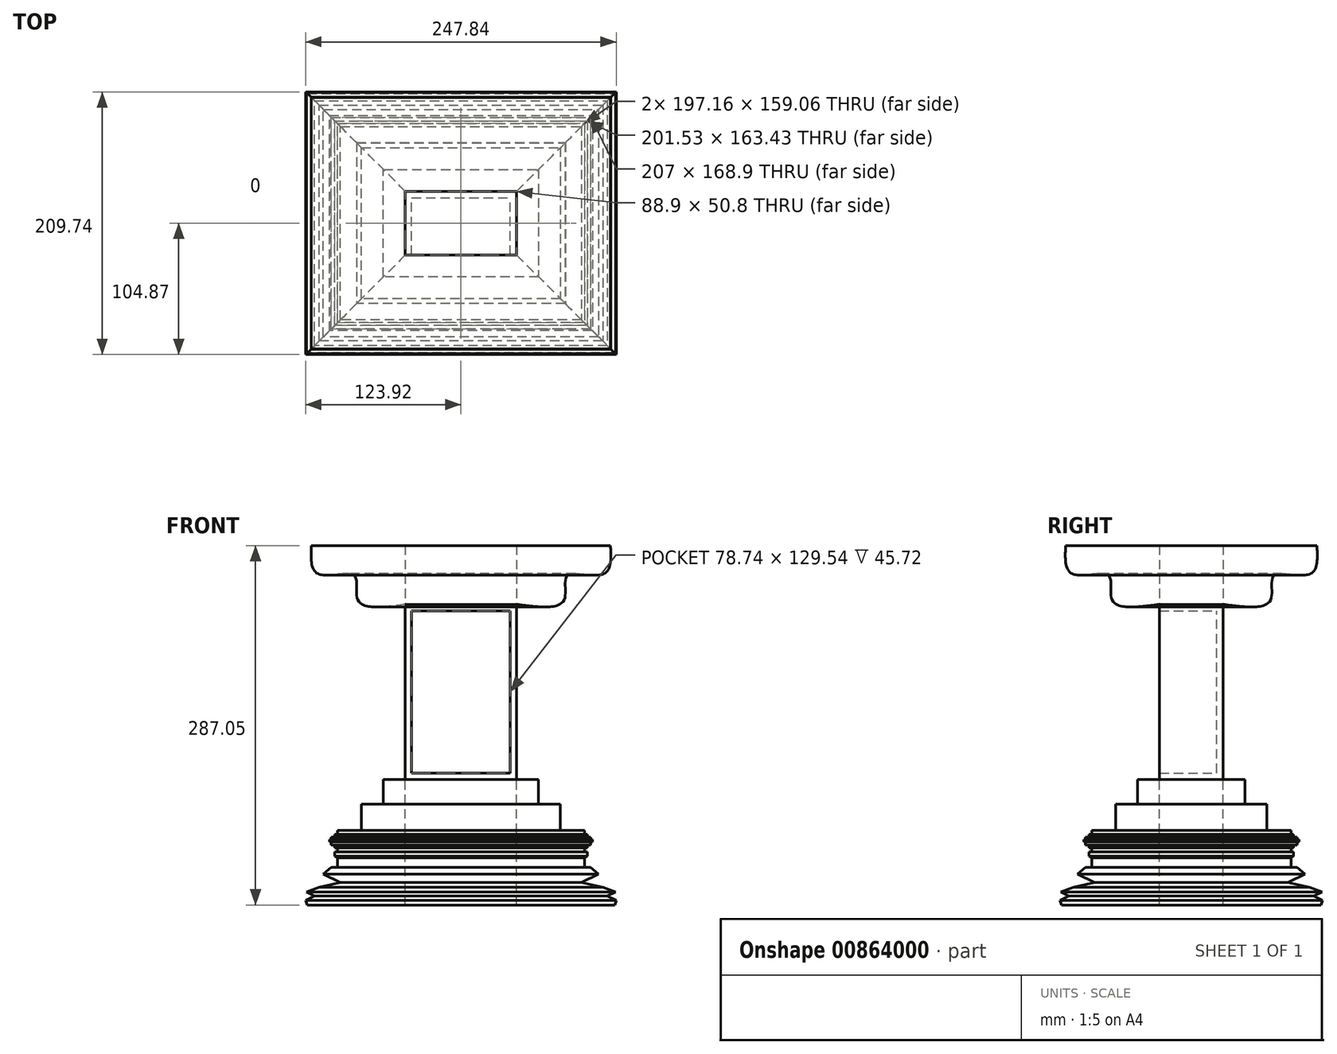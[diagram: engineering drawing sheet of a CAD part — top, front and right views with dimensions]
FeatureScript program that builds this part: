
annotation { "Feature Type Name" : "Feature", "Feature Type Description" : "" }
export const myFeature = defineFeature(function(context is Context, id is Id, definition is map)
    precondition{}
    {
        {
            var Q0;
            Q0=qCreatedBy(makeId("Front.planeOp"),FACE);
            var sketch = newSketch(context, id + "F0", { "sketchPlane" : qUnion([Q0])});
            skLineSegment(sketch, "E0.bottom", {"start": v(0, 0) * mm, "end": v(88.9, 0) * mm});
            skLineSegment(sketch, "E0.top", {"start": v(0, 139.7) * mm, "end": v(88.9, 139.7) * mm});
            skLineSegment(sketch, "E0.left", {"start": v(0, 0) * mm, "end": v(0, 139.7) * mm});
            skLineSegment(sketch, "E0.right", {"start": v(88.9, 0) * mm, "end": v(88.9, 139.7) * mm});
            skSolve(sketch);
        }
        {
            var Q0;
            Q0=makeQuery(id+"F0.imprint","IMPRINT",FACE,{"disambiguationData":[TD([[makeQuery(id+"F0.imprint","IMPRINT",EDGE,{"derivedFrom":sQuery(id+"F0.wireOp",EDGE,"E0.bottom")}),1.0]])]});
            extrude(context, id + "F1", {"entities" : qUnion([Q0]), "depth" : 50.8 * mm, "offsetDistance" : 25.4 * mm});
        }
        {
            var Q0;
            Q0=makeQuery(id+"F1.opExtrude","CAP_FACE",FACE,{"disambiguationData":[OSD([sQuery(id+"F0.wireOp",EDGE,"E0.bottom"),sQuery(id+"F0.wireOp",EDGE,"E0.top"),sQuery(id+"F0.wireOp",EDGE,"E0.left"),sQuery(id+"F0.wireOp",EDGE,"E0.right")])],"isStart":false});
            shell(context, id + "F2", {"entities" : qUnion([Q0]), "thickness" : 5.08 * mm});
        }
        {
            var Q0;
            Q0=makeQuery(id+"F1.opExtrude","SWEPT_FACE",FACE,{"disambiguationData":[OSD([sQuery(id+"F0.wireOp",EDGE,"E0.top")])]});
            var sketch = newSketch(context, id + "F3", { "sketchPlane" : qUnion([Q0])});
            skLineSegment(sketch, "E1", {"start": v(0, 0) * mm, "end": v(0, -50.8) * mm});
            skLineSegment(sketch, "E2", {"start": v(0, -50.8) * mm, "end": v(88.9, -50.8) * mm});
            skLineSegment(sketch, "E3", {"start": v(88.9, -50.8) * mm, "end": v(88.9, 0) * mm});
            skSolve(sketch);
        }
        {
            var Q0;
            Q0=makeQuery(id+"F1.opExtrude","CAP_FACE",FACE,{"disambiguationData":[OSD([sQuery(id+"F0.wireOp",EDGE,"E0.bottom"),sQuery(id+"F0.wireOp",EDGE,"E0.top"),sQuery(id+"F0.wireOp",EDGE,"E0.left"),sQuery(id+"F0.wireOp",EDGE,"E0.right")])],"isStart":true});
            var sketch = newSketch(context, id + "F4", { "sketchPlane" : qUnion([Q0])});
            skLineSegment(sketch, "E4", {"start": v(0, 139.7) * mm, "end": v(0, 186.72) * mm});
            skLineSegment(sketch, "E5", {"start": v(0, 186.72) * mm, "end": v(74.9, 186.72) * mm});
            skFitSpline(sketch, "E6", {"points": [v(74.9, 186.72) * mm, v(69.2, 163.94) * mm, v(40.73, 162.75) * mm, v(37.73, 142.97) * mm, v(0, 139.7) * mm], "startDerivative": vector(6.69, -129.44) * mm, "endDerivative": vector(-171.26, 22.05) * mm});
            skSolve(sketch);
        }
        {
            var Q0;
            Q0=makeQuery(id+"F4.imprint","IMPRINT",FACE,{"disambiguationData":[TD([[makeQuery(id+"F4.imprint","IMPRINT",EDGE,{"derivedFrom":sQuery(id+"F4.wireOp",EDGE,"E4")}),-1.0]])]});
            var Q1;
            Q1=sQuery(id+"F3.wireOp",EDGE,"E1");
            var Q2;
            Q2=sQuery(id+"F3.wireOp",EDGE,"E2");
            var Q3;
            Q3=sQuery(id+"F3.wireOp",EDGE,"E3");
            var Q4;
            Q4=makeQuery(id+"F1.opExtrude","CAP_EDGE",EDGE,{"disambiguationData":[OSD([sQuery(id+"F0.wireOp",EDGE,"E0.top")])],"isStart":true});
            sweep(context, id + "F5", {"profiles" : qUnion([Q0]), "path" : qUnion([Q1, Q2, Q3, Q4])});
        }
        {
            var Q0;
            Q0=makeQuery(id+"F1.opExtrude","CAP_FACE",FACE,{"disambiguationData":[OSD([sQuery(id+"F0.wireOp",EDGE,"E0.bottom"),sQuery(id+"F0.wireOp",EDGE,"E0.top"),sQuery(id+"F0.wireOp",EDGE,"E0.left"),sQuery(id+"F0.wireOp",EDGE,"E0.right")])],"isStart":true});
            var sketch = newSketch(context, id + "F6", { "sketchPlane" : qUnion([Q0])});
            skLineSegment(sketch, "E7", {"start": v(-88.9, 0) * mm, "end": v(-88.9, -100.33) * mm});
            skLineSegment(sketch, "E8", {"start": v(-88.9, -100.33) * mm, "end": v(-167.1, -100.33) * mm});
            skLineSegment(sketch, "E9", {"start": v(-88.9, 0) * mm, "end": v(-106.39, 0) * mm});
            skLineSegment(sketch, "E10", {"start": v(-106.39, 0) * mm, "end": v(-106.39, -19.94) * mm});
            skLineSegment(sketch, "E11", {"start": v(-106.39, -19.94) * mm, "end": v(-123.89, -19.94) * mm});
            skLineSegment(sketch, "E12", {"start": v(-123.89, -19.94) * mm, "end": v(-123.89, -40.9) * mm});
            skLineSegment(sketch, "E13", {"start": v(-123.89, -40.9) * mm, "end": v(-143.03, -40.9) * mm});
            skLineSegment(sketch, "E14", {"start": v(-143.03, -40.9) * mm, "end": v(-143.03, -44) * mm});
            skLineSegment(sketch, "E15", {"start": v(-143.03, -44) * mm, "end": v(-145.22, -44) * mm});
            skLineSegment(sketch, "E16", {"start": v(-145.22, -44) * mm, "end": v(-145.22, -46) * mm});
            skLineSegment(sketch, "E17", {"start": v(-145.22, -46) * mm, "end": v(-147.95, -46) * mm});
            skLineSegment(sketch, "E18", {"start": v(-147.95, -46) * mm, "end": v(-147.95, -48.01) * mm});
            skLineSegment(sketch, "E19", {"start": v(-147.95, -48.01) * mm, "end": v(-149.4, -48.01) * mm});
            skLineSegment(sketch, "E20", {"start": v(-149.4, -48.01) * mm, "end": v(-149.4, -50.02) * mm});
            skLineSegment(sketch, "E21", {"start": v(-149.4, -50.02) * mm, "end": v(-147.95, -50.02) * mm});
            skLineSegment(sketch, "E22", {"start": v(-147.95, -50.02) * mm, "end": v(-147.95, -52.39) * mm});
            skLineSegment(sketch, "E23", {"start": v(-147.95, -52.39) * mm, "end": v(-145.22, -52.39) * mm});
            skLineSegment(sketch, "E24", {"start": v(-145.22, -52.39) * mm, "end": v(-145.22, -54.58) * mm});
            skLineSegment(sketch, "E25", {"start": v(-145.22, -54.58) * mm, "end": v(-143.03, -54.58) * mm});
            skLineSegment(sketch, "E26", {"start": v(-143.03, -54.58) * mm, "end": v(-143.03, -58.04) * mm});
            skLineSegment(sketch, "E27", {"start": v(-143.03, -58.04) * mm, "end": v(-145.22, -58.04) * mm});
            skLineSegment(sketch, "E28", {"start": v(-145.22, -58.04) * mm, "end": v(-145.22, -61.32) * mm});
            skLineSegment(sketch, "E29", {"start": v(-145.22, -61.32) * mm, "end": v(-143.03, -62.78) * mm});
            skLineSegment(sketch, "E30", {"start": v(-143.03, -62.78) * mm, "end": v(-143.03, -70.44) * mm});
            skLineSegment(sketch, "E31", {"start": v(-143.03, -70.44) * mm, "end": v(-147.95, -70.44) * mm});
            skLineSegment(sketch, "E32", {"start": v(-147.95, -70.44) * mm, "end": v(-154.33, -75.72) * mm});
            skLineSegment(sketch, "E33", {"start": v(-154.33, -75.72) * mm, "end": v(-140.66, -82.29) * mm});
            skLineSegment(sketch, "E34", {"start": v(-140.66, -82.29) * mm, "end": v(-157.61, -86.11) * mm});
            skLineSegment(sketch, "E35", {"start": v(-157.61, -86.11) * mm, "end": v(-167.82, -90.12) * mm});
            skLineSegment(sketch, "E36", {"start": v(-167.82, -90.12) * mm, "end": v(-161.26, -93.04) * mm});
            skLineSegment(sketch, "E37", {"start": v(-161.26, -93.04) * mm, "end": v(-168.37, -96.69) * mm});
            skLineSegment(sketch, "E38", {"start": v(-168.37, -96.69) * mm, "end": v(-167.1, -100.33) * mm});
            skSolve(sketch);
        }
        {
            var Q0;
            Q0=makeQuery(id+"F6.imprint","IMPRINT",FACE,{"disambiguationData":[TD([[makeQuery(id+"F6.imprint","IMPRINT",EDGE,{"derivedFrom":sQuery(id+"F6.wireOp",EDGE,"E7")}),-1.0]])]});
            var Q1;
            Q1=makeQuery(id+"F1.opExtrude","CAP_EDGE",EDGE,{"disambiguationData":[OSD([sQuery(id+"F0.wireOp",EDGE,"E0.bottom")])],"isStart":true});
            var Q2;
            Q2=makeQuery(id+"F1.opExtrude","SWEPT_EDGE",EDGE,{"disambiguationData":[OSD([sQuery(id+"F0.wireOp",EDGE,"E0.bottom"),sQuery(id+"F0.wireOp",EDGE,"E0.left")])]});
            var Q3;
            Q3=makeQuery(id+"F1.opExtrude","CAP_EDGE",EDGE,{"disambiguationData":[OSD([sQuery(id+"F0.wireOp",EDGE,"E0.bottom")])],"isStart":false});
            var Q4;
            Q4=makeQuery(id+"F1.opExtrude","SWEPT_EDGE",EDGE,{"disambiguationData":[OSD([sQuery(id+"F0.wireOp",EDGE,"E0.bottom"),sQuery(id+"F0.wireOp",EDGE,"E0.right")])]});
            sweep(context, id + "F7", {"profiles" : qUnion([Q0]), "path" : qUnion([Q1, Q2, Q3, Q4])});
        }
    });
